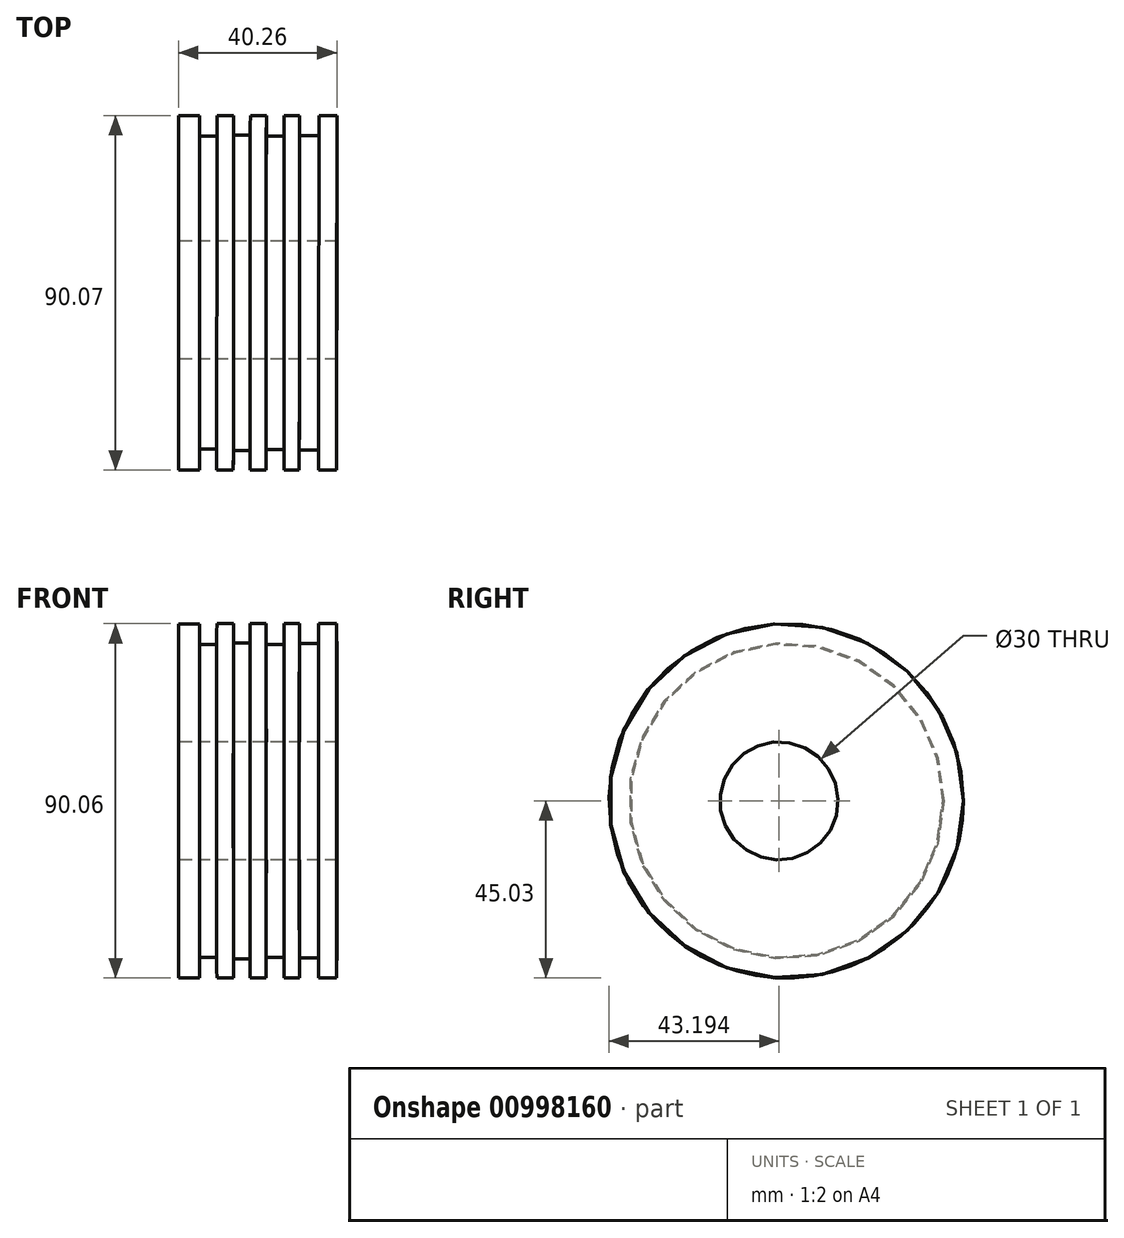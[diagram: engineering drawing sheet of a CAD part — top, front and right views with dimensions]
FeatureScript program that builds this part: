
annotation { "Feature Type Name" : "Feature", "Feature Type Description" : "" }
export const myFeature = defineFeature(function(context is Context, id is Id, definition is map)
    precondition{}
    {
        {
            var Q0;
            Q0=qCreatedBy(makeId("Top.planeOp"),FACE);
            var sketch = newSketch(context, id + "F0", { "sketchPlane" : qUnion([Q0])});
            skCircle(sketch, "E0", {"center": v(112.13, 84.93) * mm, "radius": 50 * mm});
            skCircle(sketch, "E1", {"center": v(112.13, 84.93) * mm, "radius": 15 * mm});
            skLineSegment(sketch, "E2", {"start": v(196.26, -55.92) * mm, "end": v(196.26, -10.92) * mm});
            skLineSegment(sketch, "E3", {"start": v(196.26, -10.92) * mm, "end": v(201.58, -10.92) * mm});
            skLineSegment(sketch, "E4", {"start": v(201.58, -10.92) * mm, "end": v(201.58, -16.16) * mm});
            skLineSegment(sketch, "E5", {"start": v(201.58, -16.16) * mm, "end": v(205.98, -16.16) * mm});
            skLineSegment(sketch, "E6", {"start": v(205.98, -16.16) * mm, "end": v(205.98, -10.92) * mm});
            skLineSegment(sketch, "E7", {"start": v(205.98, -10.92) * mm, "end": v(210.2, -10.92) * mm});
            skLineSegment(sketch, "E8", {"start": v(210.2, -10.92) * mm, "end": v(210.2, -15.82) * mm});
            skLineSegment(sketch, "E9", {"start": v(210.2, -15.82) * mm, "end": v(214.44, -15.82) * mm});
            skLineSegment(sketch, "E10", {"start": v(214.44, -15.82) * mm, "end": v(214.44, -10.92) * mm});
            skLineSegment(sketch, "E11", {"start": v(214.44, -10.92) * mm, "end": v(218.5, -10.92) * mm});
            skLineSegment(sketch, "E12", {"start": v(218.5, -10.92) * mm, "end": v(218.5, -16.16) * mm});
            skLineSegment(sketch, "E13", {"start": v(218.5, -16.16) * mm, "end": v(223.06, -16.16) * mm});
            skLineSegment(sketch, "E14", {"start": v(223.06, -16.16) * mm, "end": v(223.06, -10.92) * mm});
            skLineSegment(sketch, "E15", {"start": v(223.06, -10.92) * mm, "end": v(226.95, -10.92) * mm});
            skLineSegment(sketch, "E16", {"start": v(226.95, -10.92) * mm, "end": v(226.95, -15.99) * mm});
            skLineSegment(sketch, "E17", {"start": v(226.95, -15.99) * mm, "end": v(231.86, -15.99) * mm});
            skLineSegment(sketch, "E18", {"start": v(231.86, -15.99) * mm, "end": v(231.86, -10.92) * mm});
            skLineSegment(sketch, "E19", {"start": v(231.86, -10.92) * mm, "end": v(236.43, -10.92) * mm});
            skLineSegment(sketch, "E20", {"start": v(236.43, -10.92) * mm, "end": v(236.43, -55.96) * mm});
            skLineSegment(sketch, "E21", {"start": v(236.43, -55.96) * mm, "end": v(196.26, -55.92) * mm});
            skSolve(sketch);
        }
        {
            var Q0;
            Q0=makeQuery(id+"F0.imprint","IMPRINT",FACE,{"disambiguationData":[TD([[makeQuery(id+"F0.imprint","IMPRINT",EDGE,{"derivedFrom":sQuery(id+"F0.wireOp",EDGE,"E2")}),-1.0]])]});
            var Q1;
            Q1=sQuery(id+"F0.wireOp",EDGE,"E21");
            revolve(context, id + "F1", {"surfaceOperationType" : NewSurfaceOperationType.NEW, "entities" : qUnion([Q0]), "axis" : qUnion([Q1]), "revolveType" : RevolveType.FULL});
        }
        {
            var Q0;
            Q0=qCreatedBy(makeId("Right.planeOp"),FACE);
            var sketch = newSketch(context, id + "F2", { "sketchPlane" : qUnion([Q0])});
            skCircle(sketch, "E22", {"center": v(-57.8, 0) * mm, "radius": 15 * mm});
            skSolve(sketch);
        }
        {
            var Q0;
            Q0=sQuery(id+"F2.wireOp",VERTEX,"E22.center");
            var Q1;
            Q1=makeQuery(id+"F1.opRevolve","SWEPT_BODY",BODY,{"disambiguationData":[OSD([sQuery(id+"F0.wireOp",EDGE,"E2"),sQuery(id+"F0.wireOp",EDGE,"E3"),sQuery(id+"F0.wireOp",EDGE,"E4"),sQuery(id+"F0.wireOp",EDGE,"E5"),sQuery(id+"F0.wireOp",EDGE,"E6"),sQuery(id+"F0.wireOp",EDGE,"E7"),sQuery(id+"F0.wireOp",EDGE,"E8"),sQuery(id+"F0.wireOp",EDGE,"E9"),sQuery(id+"F0.wireOp",EDGE,"E10"),sQuery(id+"F0.wireOp",EDGE,"E11"),sQuery(id+"F0.wireOp",EDGE,"E12"),sQuery(id+"F0.wireOp",EDGE,"E13"),sQuery(id+"F0.wireOp",EDGE,"E14"),sQuery(id+"F0.wireOp",EDGE,"E15"),sQuery(id+"F0.wireOp",EDGE,"E16"),sQuery(id+"F0.wireOp",EDGE,"E17"),sQuery(id+"F0.wireOp",EDGE,"E18"),sQuery(id+"F0.wireOp",EDGE,"E19"),sQuery(id+"F0.wireOp",EDGE,"E20"),sQuery(id+"F0.wireOp",EDGE,"E21")])]});
            hole(context, id + "F3", {"style" : HoleStyle.SIMPLE, "endStyle" : HoleEndStyle.BLIND, "oppositeDirection" : true, "holeDiameter" : 30 * mm, "majorDiameter" : 5 * mm, "holeDepth" : 100 * mm, "isTappedThrough" : true, "tappedDepth" : 12 * mm, "tapClearance" : 3, "locations" : qUnion([Q0]), "scope" : qUnion([Q1])});
        }
    });
